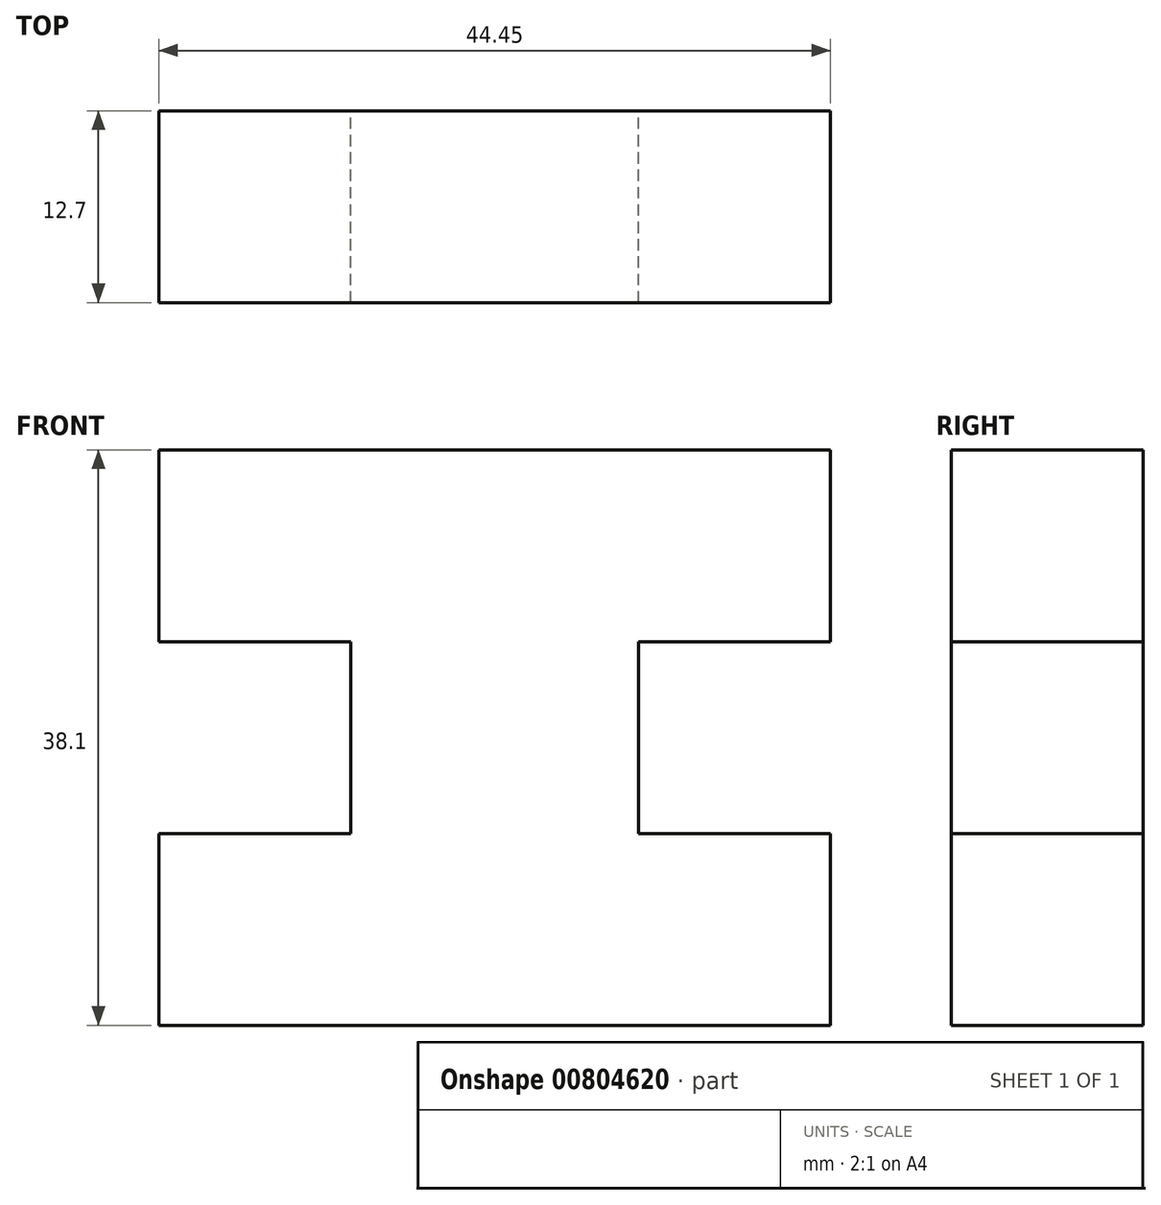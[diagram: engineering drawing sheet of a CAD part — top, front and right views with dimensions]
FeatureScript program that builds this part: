
annotation { "Feature Type Name" : "Feature", "Feature Type Description" : "" }
export const myFeature = defineFeature(function(context is Context, id is Id, definition is map)
    precondition{}
    {
        {
            var Q0;
            Q0=qCreatedBy(makeId("Front.planeOp"),FACE);
            var sketch = newSketch(context, id + "F0", { "sketchPlane" : qUnion([Q0])});
            skLineSegment(sketch, "E0", {"start": v(0, 0) * mm, "end": v(44.45, 0) * mm});
            skLineSegment(sketch, "E1", {"start": v(44.45, 0) * mm, "end": v(44.45, 12.7) * mm});
            skLineSegment(sketch, "E2", {"start": v(44.45, 12.7) * mm, "end": v(31.75, 12.7) * mm});
            skLineSegment(sketch, "E3", {"start": v(31.75, 12.7) * mm, "end": v(31.75, 25.4) * mm});
            skLineSegment(sketch, "E4", {"start": v(31.75, 25.4) * mm, "end": v(44.45, 25.4) * mm});
            skLineSegment(sketch, "E5", {"start": v(44.45, 25.4) * mm, "end": v(44.45, 38.1) * mm});
            skLineSegment(sketch, "E6", {"start": v(44.45, 38.1) * mm, "end": v(0, 38.1) * mm});
            skLineSegment(sketch, "E7", {"start": v(0, 38.1) * mm, "end": v(0, 25.4) * mm});
            skLineSegment(sketch, "E8", {"start": v(0, 25.4) * mm, "end": v(12.7, 25.4) * mm});
            skLineSegment(sketch, "E9", {"start": v(12.7, 25.4) * mm, "end": v(12.7, 12.7) * mm});
            skLineSegment(sketch, "E10", {"start": v(12.7, 12.7) * mm, "end": v(0, 12.7) * mm});
            skLineSegment(sketch, "E11", {"start": v(0, 12.7) * mm, "end": v(0, 0) * mm});
            skSolve(sketch);
        }
        {
            var Q0;
            Q0 = qSketchRegion(id + "F0", true);
            var Q1;
            Q1=makeQuery(id+"F0.imprint","IMPRINT",FACE,{"disambiguationData":[TD([[makeQuery(id+"F0.imprint","IMPRINT",EDGE,{"derivedFrom":sQuery(id+"F0.wireOp",EDGE,"E0")}),1.0]])]});
            extrude(context, id + "F1", {"entities" : qUnion([Q0, Q1]), "depth" : 12.7 * mm, "offsetDistance" : 25.4 * mm});
        }
    });
